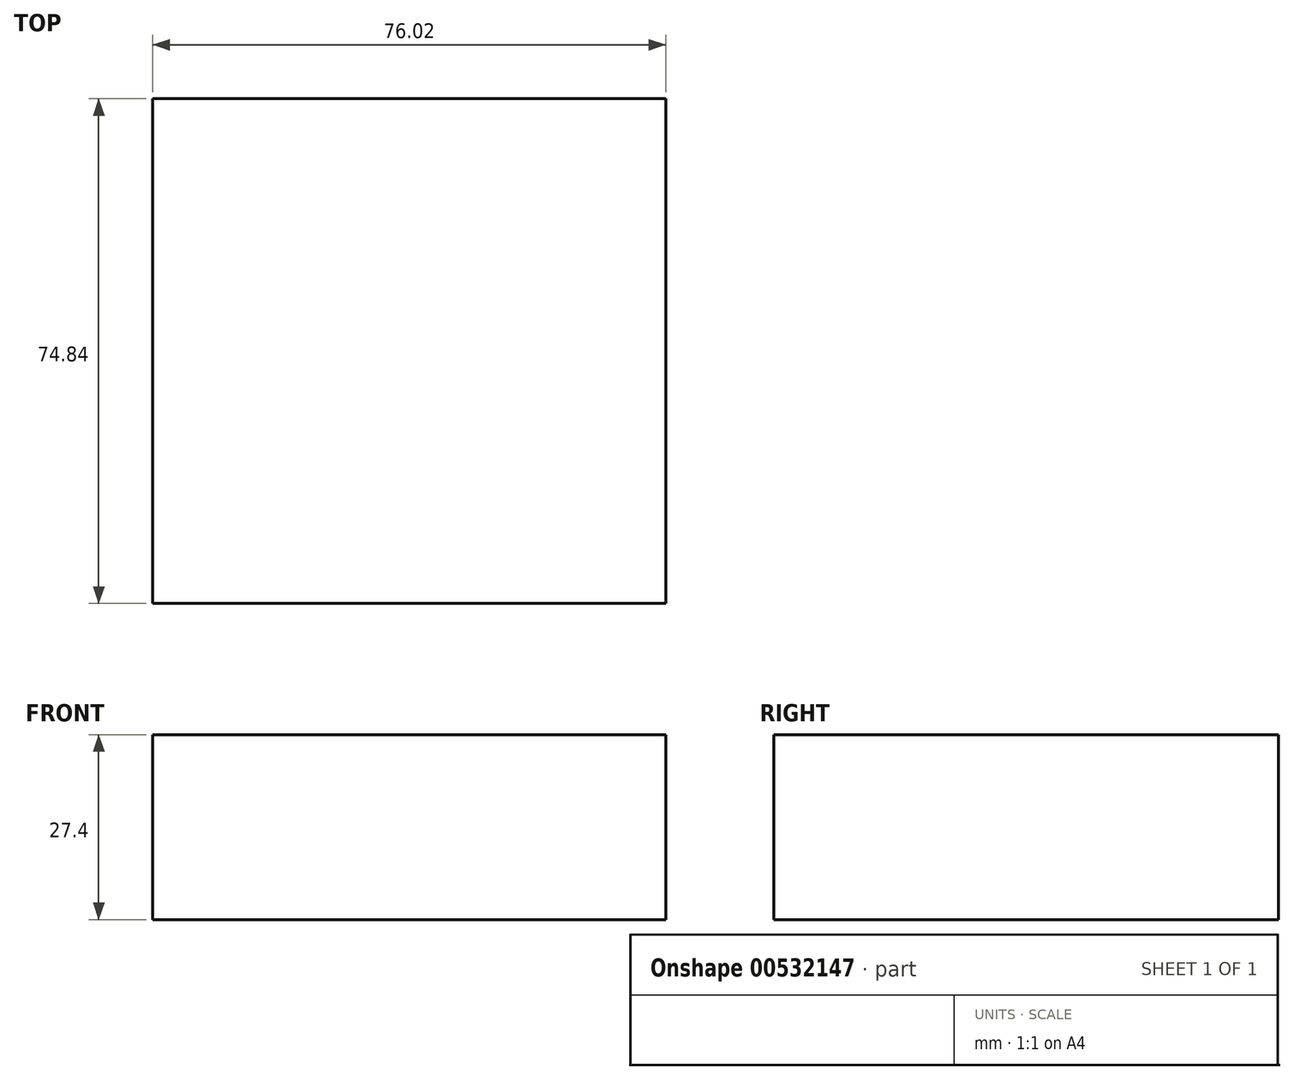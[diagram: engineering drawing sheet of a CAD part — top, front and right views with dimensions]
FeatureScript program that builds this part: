
annotation { "Feature Type Name" : "Feature", "Feature Type Description" : "" }
export const myFeature = defineFeature(function(context is Context, id is Id, definition is map)
    precondition{}
    {
        {
            var Q0;
            Q0=qCreatedBy(makeId("Top.planeOp"),FACE);
            var sketch = newSketch(context, id + "F0", { "sketchPlane" : qUnion([Q0])});
            skLineSegment(sketch, "E0.bottom", {"start": v(76.02, 74.84) * mm, "end": v(0, 74.84) * mm});
            skLineSegment(sketch, "E0.top", {"start": v(76.02, 0) * mm, "end": v(0, 0) * mm});
            skLineSegment(sketch, "E0.left", {"start": v(76.02, 74.84) * mm, "end": v(76.02, 0) * mm});
            skLineSegment(sketch, "E0.right", {"start": v(0, 74.84) * mm, "end": v(0, 0) * mm});
            skSolve(sketch);
        }
        {
            var Q0;
            Q0 = qSketchRegion(id + "F0", true);
            var Q1;
            Q1=makeQuery(id+"F0.imprint","IMPRINT",FACE,{"disambiguationData":[TD([[makeQuery(id+"F0.imprint","IMPRINT",EDGE,{"derivedFrom":sQuery(id+"F0.wireOp",EDGE,"E0.bottom")}),1.0]])]});
            extrude(context, id + "F1", {"entities" : qUnion([Q0, Q1]), "depth" : 25.4 * mm, "offsetDistance" : 25.4 * mm});
        }
        {
            var Q0;
            Q0=makeQuery(id+"F1.opExtrude","CAP_FACE",FACE,{"disambiguationData":[OSD([sQuery(id+"F0.wireOp",EDGE,"E0.bottom"),sQuery(id+"F0.wireOp",EDGE,"E0.top"),sQuery(id+"F0.wireOp",EDGE,"E0.left"),sQuery(id+"F0.wireOp",EDGE,"E0.right")])],"isStart":false});
            extrude(context, id + "F2", {"entities" : qUnion([Q0]), "operationType" : NewBodyOperationType.ADD, "depth" : 2 * mm, "offsetDistance" : 25.4 * mm});
        }
    });
